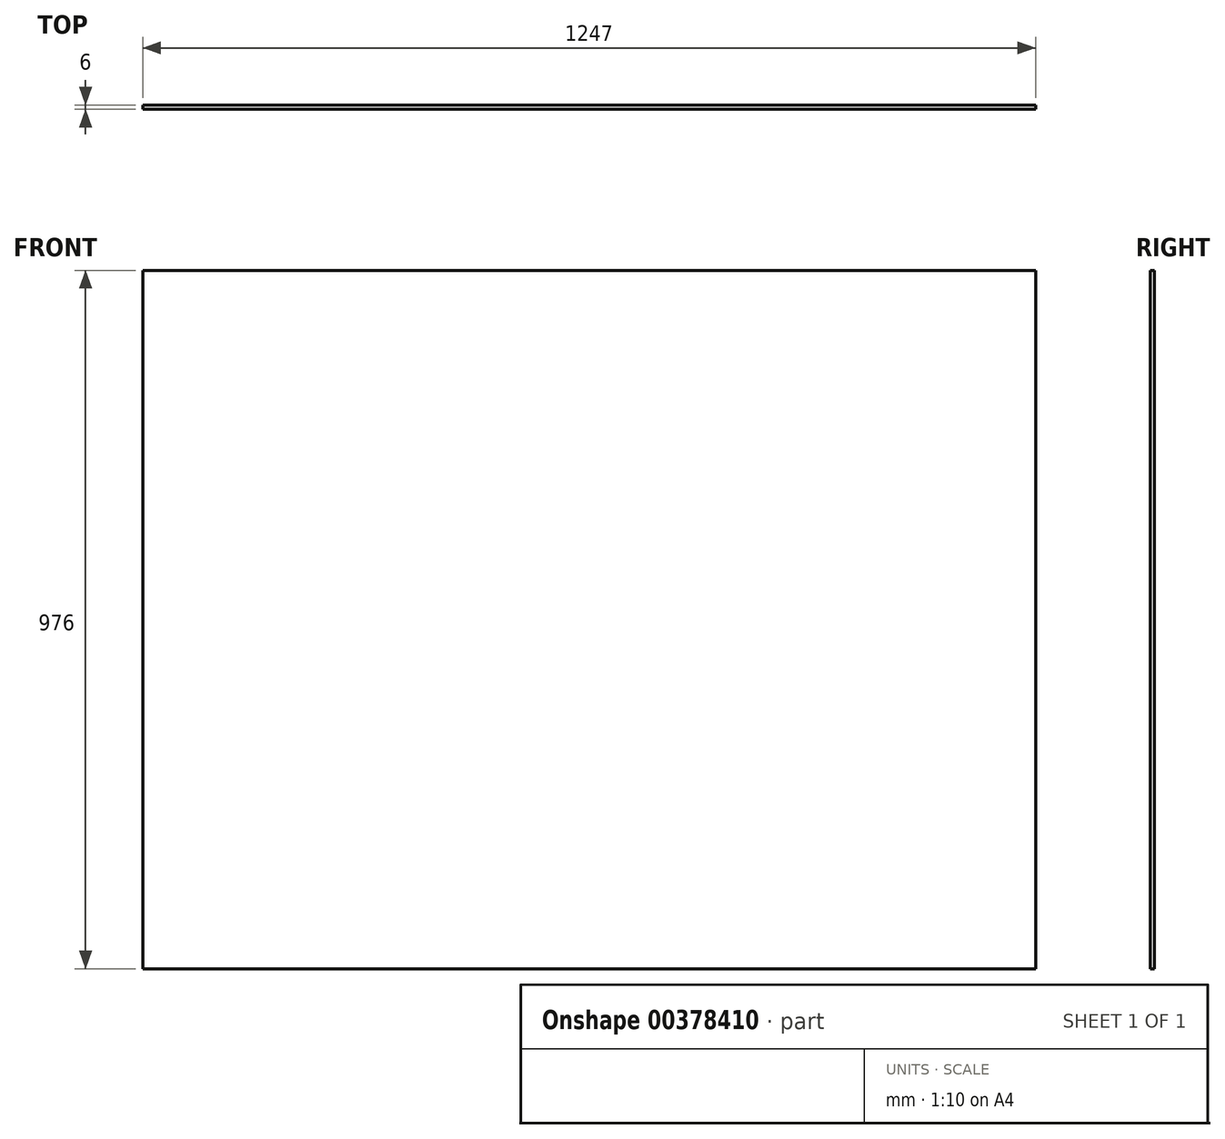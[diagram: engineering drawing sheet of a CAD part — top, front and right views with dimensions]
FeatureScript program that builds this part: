
annotation { "Feature Type Name" : "Feature", "Feature Type Description" : "" }
export const myFeature = defineFeature(function(context is Context, id is Id, definition is map)
    precondition{}
    {
        {
            var Q0;
            Q0=qCreatedBy(makeId("Front.planeOp"),FACE);
            var sketch = newSketch(context, id + "F0", { "sketchPlane" : qUnion([Q0])});
            skLineSegment(sketch, "E0.bottom", {"start": v(623.5, 488) * mm, "end": v(-623.5, 488) * mm});
            skLineSegment(sketch, "E0.top", {"start": v(623.5, -488) * mm, "end": v(-623.5, -488) * mm});
            skLineSegment(sketch, "E0.left", {"start": v(623.5, 488) * mm, "end": v(623.5, -488) * mm});
            skLineSegment(sketch, "E0.right", {"start": v(-623.5, 488) * mm, "end": v(-623.5, -488) * mm});
            skPoint(sketch, "E0.middle", {"position": v(0, 0) * mm});
            skSolve(sketch);
        }
        {
            var Q0;
            Q0 = qSketchRegion(id + "F0", true);
            extrude(context, id + "F1", {"entities" : qUnion([Q0]), "depth" : 6 * mm});
        }
    });
